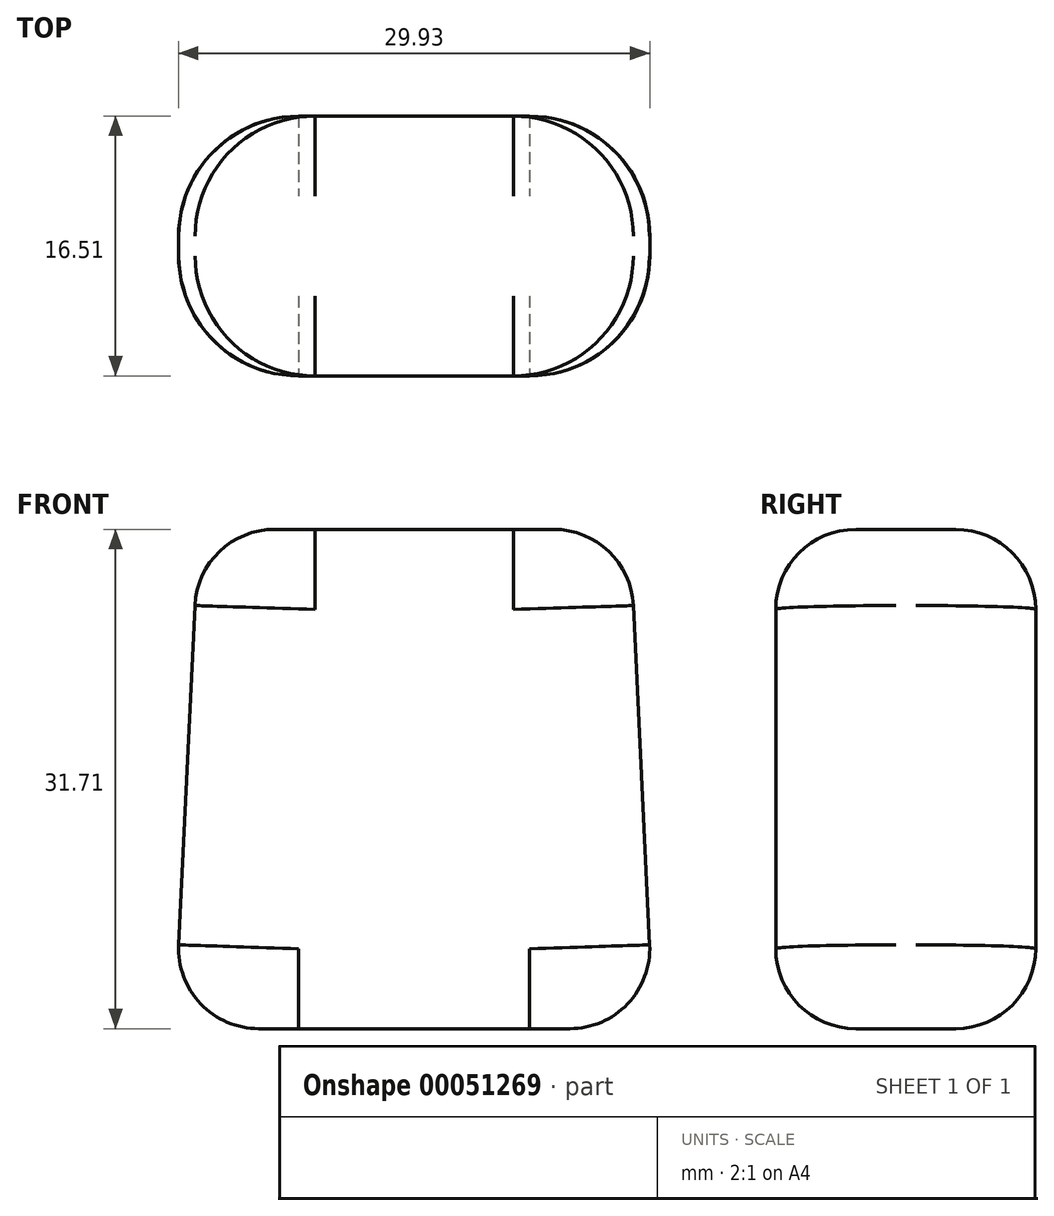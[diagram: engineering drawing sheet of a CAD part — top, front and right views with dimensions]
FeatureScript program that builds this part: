
annotation { "Feature Type Name" : "Feature", "Feature Type Description" : "" }
export const myFeature = defineFeature(function(context is Context, id is Id, definition is map)
    precondition{}
    {
        {
            var Q0;
            Q0=qCreatedBy(makeId("Front.planeOp"),FACE);
            var sketch = newSketch(context, id + "F0", { "sketchPlane" : qUnion([Q0])});
            skLineSegment(sketch, "E0", {"start": v(-15.36, 0) * mm, "end": v(15.06, 0) * mm});
            skLineSegment(sketch, "E1", {"start": v(-15.36, 0) * mm, "end": v(-13.85, 31.71) * mm});
            skLineSegment(sketch, "E2", {"start": v(-13.85, 31.71) * mm, "end": v(13.54, 31.71) * mm});
            skLineSegment(sketch, "E3", {"start": v(13.54, 31.71) * mm, "end": v(15.06, 0) * mm});
            skSolve(sketch);
        }
        {
            var Q0;
            Q0=makeQuery(id+"F0.imprint","IMPRINT",FACE,{"disambiguationData":[TD([[makeQuery(id+"F0.imprint","IMPRINT",EDGE,{"derivedFrom":sQuery(id+"F0.wireOp",EDGE,"E0")}),1.0]])]});
            extrude(context, id + "F1", {"entities" : qUnion([Q0]), "depth" : 16.5 * mm});
        }
        {
            var Q0;
            Q0=makeQuery(id+"F1.opExtrude","CAP_EDGE",EDGE,{"disambiguationData":[OSD([sQuery(id+"F0.wireOp",EDGE,"E1")])],"isStart":false});
            fillet(context, id + "F2", {"entities" : qUnion([Q0]), "radius" : 7.62 * mm, "tangentPropagation" : true, "allowEdgeOverflow" : false});
        }
        {
            var Q0;
            Q0=makeQuery(id+"F1.opExtrude","CAP_EDGE",EDGE,{"disambiguationData":[OSD([sQuery(id+"F0.wireOp",EDGE,"E3")])],"isStart":false});
            var Q1;
            Q1=makeQuery(id+"F1.opExtrude","CAP_EDGE",EDGE,{"disambiguationData":[OSD([sQuery(id+"F0.wireOp",EDGE,"E3")])],"isStart":true});
            var Q2;
            Q2=makeQuery(id+"F1.opExtrude","CAP_EDGE",EDGE,{"disambiguationData":[OSD([sQuery(id+"F0.wireOp",EDGE,"E1")])],"isStart":true});
            fillet(context, id + "F3", {"entities" : qUnion([Q0, Q1, Q2]), "radius" : 7.62 * mm, "tangentPropagation" : true, "allowEdgeOverflow" : false});
        }
        {
            var Q0;
            Q0=makeQuery(id+"F1.opExtrude","CAP_EDGE",EDGE,{"disambiguationData":[OSD([sQuery(id+"F0.wireOp",EDGE,"E0")])],"isStart":true});
            fillet(context, id + "F4", {"entities" : qUnion([Q0]), "radius" : 5.08 * mm, "tangentPropagation" : true, "allowEdgeOverflow" : false});
        }
        {
            var Q0;
            Q0=makeQuery(id+"F1.opExtrude","CAP_EDGE",EDGE,{"disambiguationData":[OSD([sQuery(id+"F0.wireOp",EDGE,"E2")])],"isStart":false});
            fillet(context, id + "F5", {"entities" : qUnion([Q0]), "radius" : 5.08 * mm, "tangentPropagation" : true, "allowEdgeOverflow" : false});
        }
    });
